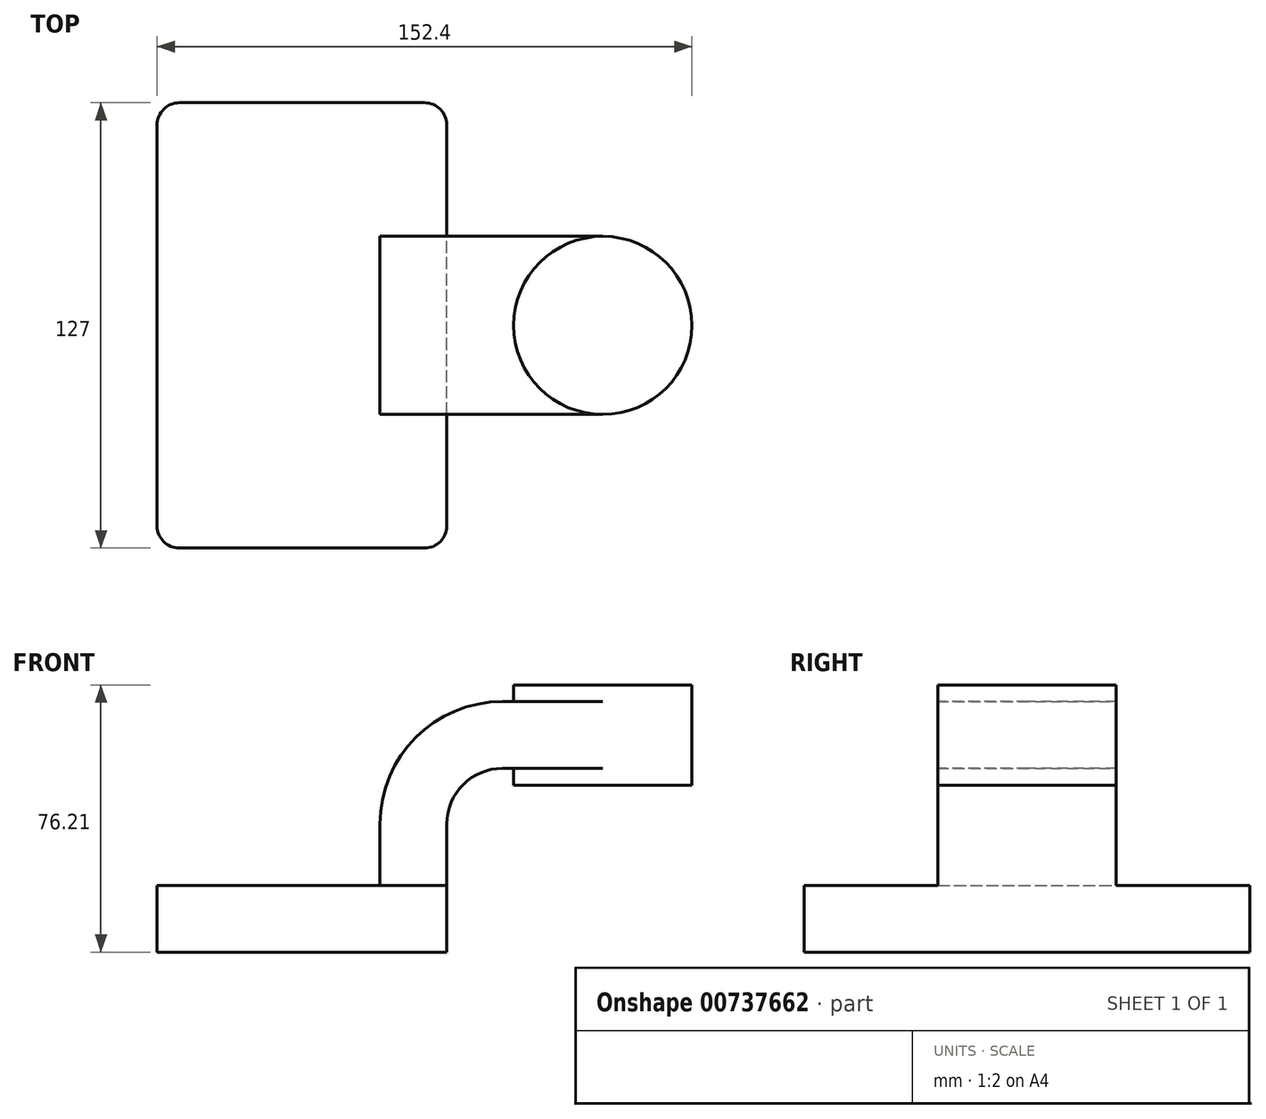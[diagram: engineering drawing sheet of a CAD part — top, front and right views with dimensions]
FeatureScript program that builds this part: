
annotation { "Feature Type Name" : "Feature", "Feature Type Description" : "" }
export const myFeature = defineFeature(function(context is Context, id is Id, definition is map)
    precondition{}
    {
        {
            var Q0;
            Q0=qCreatedBy(makeId("Front.planeOp"),FACE);
            var sketch = newSketch(context, id + "F0", { "sketchPlane" : qUnion([Q0])});
            skLineSegment(sketch, "E0.bottom", {"start": v(-41.28, 9.52) * mm, "end": v(41.28, 9.53) * mm});
            skLineSegment(sketch, "E0.top", {"start": v(-41.28, -9.53) * mm, "end": v(41.28, -9.53) * mm});
            skLineSegment(sketch, "E0.left", {"start": v(-41.28, 9.52) * mm, "end": v(-41.28, -9.53) * mm});
            skLineSegment(sketch, "E0.right", {"start": v(41.28, 9.53) * mm, "end": v(41.28, -9.52) * mm});
            skPoint(sketch, "E0.middle", {"position": v(0, 0) * mm});
            skLineSegment(sketch, "E1", {"start": v(41.27, 9.53) * mm, "end": v(41.27, 27) * mm});
            skArc(sketch, "E2", {"start": v(41.28, 27) * mm, "mid": v(45.92, 38.23) * mm, "end": v(57.15, 42.88) * mm});
            skLineSegment(sketch, "E3.bottom", {"start": v(60.32, 66.67) * mm, "end": v(111.12, 66.67) * mm});
            skLineSegment(sketch, "E3.top", {"start": v(60.33, 38.1) * mm, "end": v(111.12, 38.1) * mm});
            skLineSegment(sketch, "E3.left", {"start": v(60.32, 66.67) * mm, "end": v(60.32, 38.1) * mm});
            skLineSegment(sketch, "E3.right", {"start": v(111.12, 66.67) * mm, "end": v(111.12, 38.1) * mm});
            skPoint(sketch, "E3.middle", {"position": v(85.72, 52.39) * mm});
            skLineSegment(sketch, "E4", {"start": v(57.15, 42.88) * mm, "end": v(85.73, 42.88) * mm});
            skLineSegment(sketch, "E5.0", {"start": v(57.15, 61.93) * mm, "end": v(85.73, 61.93) * mm});
            skArc(sketch, "E5.1", {"start": v(22.23, 27) * mm, "mid": v(32.45, 51.7) * mm, "end": v(57.15, 61.93) * mm});
            skLineSegment(sketch, "E5.2", {"start": v(22.23, 9.53) * mm, "end": v(22.23, 27) * mm});
            skLineSegment(sketch, "E6", {"start": v(85.73, 42.88) * mm, "end": v(85.72, 66.67) * mm});
            skFitSpline(sketch, "E7", {"points": [v(-41.28, 9.52) * mm, v(57.15, 61.93) * mm], "startDerivative": vector(59.03, 90.81) * mm, "endDerivative": vector(155, -2.6) * mm});
            skLineSegment(sketch, "E8", {"start": v(85.73, 42.88) * mm, "end": v(85.72, 38.1) * mm});
            skSolve(sketch);
        }
        {
            var Q0;
            Q0=makeQuery(id+"F0.imprint","IMPRINT",FACE,{"disambiguationData":[TD([[makeQuery(id+"F0.imprint","IMPRINT",EDGE,{"derivedFrom":sQuery(id+"F0.wireOp",EDGE,"E0.top")}),1.0]])]});
            extrude(context, id + "F1", {"entities" : qUnion([Q0]), "endBound" : BoundingType.SYMMETRIC, "depth" : 127 * mm, "offsetDistance" : 25.4 * mm});
        }
        {
            var Q0;
            {var subQ0=sQuery(id+"F0.wireOp",EDGE,"E1");Q0=makeQuery(id+"F0.imprint","IMPRINT",FACE,{"disambiguationData":[TD([[makeQuery(id+"F0.imprint","IMPRINT",EDGE,{"derivedFrom":subQ0}),1.0]])]});}
            extrude(context, id + "F2", {"entities" : qUnion([Q0]), "operationType" : NewBodyOperationType.ADD, "endBound" : BoundingType.SYMMETRIC, "depth" : 50.8 * mm, "offsetDistance" : 25.4 * mm});
        }
        {
            var Q0;
            {var subQ0=sQuery(id+"F0.wireOp",EDGE,"E5.0");var subQ1=sQuery(id+"F0.wireOp",EDGE,"E3.left");var subQ2=makeQuery(id+"F0.imprint","INTERSECT",VERTEX,{"derivedFrom":[subQ1,subQ0]});Q0=makeQuery(id+"F0.imprint","IMPRINT",FACE,{"disambiguationData":[TD([[makeQuery(id+"F0.imprint","IMPRINT",EDGE,{"disambiguationData":[TD([[subQ2,-1.0]])],"derivedFrom":subQ1}),1.0]])]});}
            extrude(context, id + "F3", {"entities" : qUnion([Q0]), "operationType" : NewBodyOperationType.ADD, "endBound" : BoundingType.SYMMETRIC, "depth" : 50.8 * mm, "offsetDistance" : 25.4 * mm});
        }
        {
            var Q0;
            Q0=makeQuery(id+"F0.imprint","IMPRINT",FACE,{"disambiguationData":[TD([[makeQuery(id+"F0.imprint","IMPRINT",EDGE,{"derivedFrom":sQuery(id+"F0.wireOp",EDGE,"E5.1")}),1.0]])]});
            extrude(context, id + "F4", {"entities" : qUnion([Q0]), "operationType" : NewBodyOperationType.ADD, "endBound" : BoundingType.SYMMETRIC, "depth" : 15.88 * mm, "offsetDistance" : 25.4 * mm});
        }
        {
            var Q0;
            {var subQ3=sQuery(id+"F0.wireOp",EDGE,"E3.right");Q0=makeQuery(id+"F0.imprint","IMPRINT",FACE,{"disambiguationData":[TD([[makeQuery(id+"F0.imprint","IMPRINT",EDGE,{"derivedFrom":subQ3}),-1.0]])]});}
            var Q1;
            Q1=sQuery(id+"F0.wireOp",EDGE,"E6");
            revolve(context, id + "F5", {"operationType" : NewBodyOperationType.ADD, "surfaceOperationType" : NewSurfaceOperationType.NEW, "entities" : qUnion([Q0]), "axis" : qUnion([Q1]), "revolveType" : RevolveType.FULL});
        }
        {
            var Q0;
            Q0=makeQuery(id+"F1.opExtrude","CAP_EDGE",EDGE,{"disambiguationData":[OSD([sQuery(id+"F0.wireOp",EDGE,"E0.left")])],"isStart":false});
            var Q1;
            Q1=makeQuery(id+"F1.opExtrude","CAP_EDGE",EDGE,{"disambiguationData":[OSD([sQuery(id+"F0.wireOp",EDGE,"E0.right")])],"isStart":false});
            var Q2;
            Q2=makeQuery(id+"F1.opExtrude","CAP_EDGE",EDGE,{"disambiguationData":[OSD([sQuery(id+"F0.wireOp",EDGE,"E0.right")])],"isStart":true});
            var Q3;
            Q3=makeQuery(id+"F1.opExtrude","CAP_EDGE",EDGE,{"disambiguationData":[OSD([sQuery(id+"F0.wireOp",EDGE,"E0.left")])],"isStart":true});
            fillet(context, id + "F6", {"entities" : qUnion([Q0, Q1, Q2, Q3]), "radius" : 6.35 * mm, "tangentPropagation" : true, "allowEdgeOverflow" : false});
        }
    });
